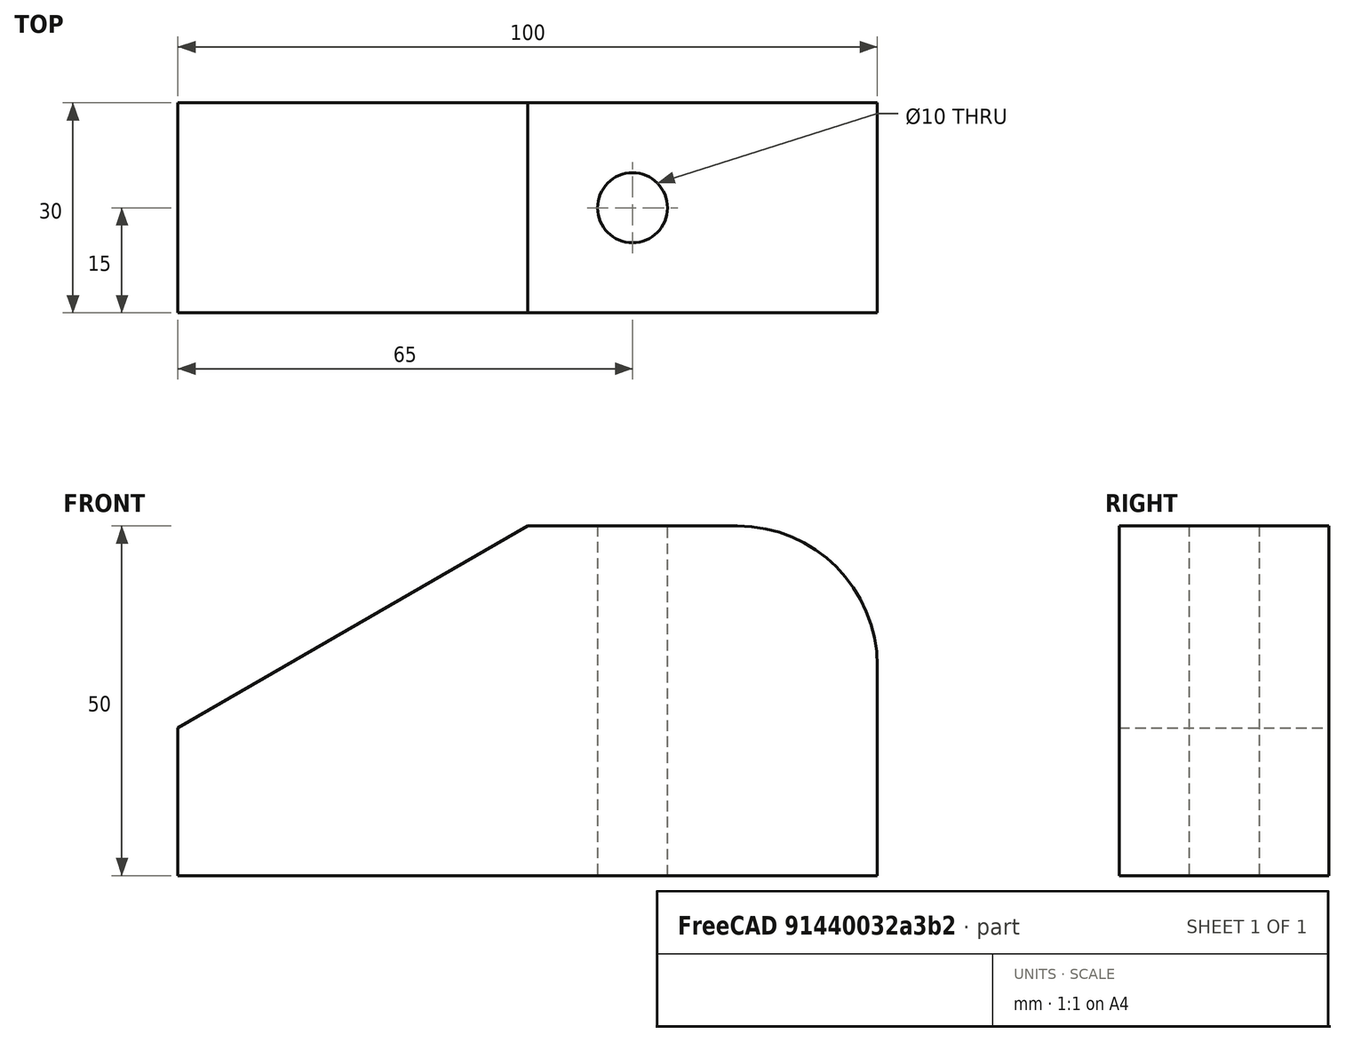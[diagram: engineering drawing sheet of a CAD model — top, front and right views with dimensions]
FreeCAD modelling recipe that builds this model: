
FCSTD DOCUMENT  (FreeCAD 0.20R29410 (Git))
Label: Creating a simple part with Part WB
License: All rights reserved
LicenseURL: http://en.wikipedia.org/wiki/All_rights_reserved
objects: Part::Box×2, Part::Cut×2, Part::Fillet×1, Part::Cylinder×1
note: 6 computed .brp shape members not serialized (recipe doc carries the construction recipe); baked Part::Feature solids carry a one-line shape summary decoded from their .brp

FEATURE [Part::Box] Box  label="Cube"
  AttacherType = Attacher::AttachEngine3D
  Height = 50
  Length = 100
  Width = 30
FEATURE [Part::Fillet] Fillet
  Base = -> Box
  Edges = 1 edges r=20: [Edge6]
FEATURE [Part::Box] Box001  label="Cube001"
  AttacherType = Attacher::AttachEngine3D
  Height = 30
  Length = 60
  Placement = pos=(0,0,21.13) rot=(0,1,0;-0.523599rad)
  Width = 30
FEATURE [Part::Cut] Cut
  Base = -> Fillet
  Tool = -> Box001
FEATURE [Part::Cylinder] Cylinder
  Angle = 360
  AttacherType = Attacher::AttachEngine3D
  FirstAngle = 0
  Height = 50
  Placement = pos=(65,15,0) rot=(0,0,1;0rad)
  Radius = 5
  SecondAngle = 0
FEATURE [Part::Cut] Cut001  label="SimplePart"
  Base = -> Cut
  Tool = -> Cylinder
